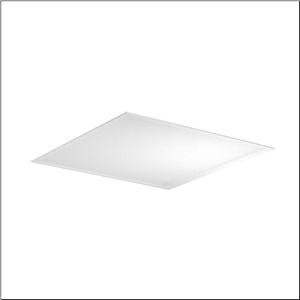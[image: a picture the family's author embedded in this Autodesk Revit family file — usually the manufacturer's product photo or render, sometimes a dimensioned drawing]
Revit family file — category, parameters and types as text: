
# Revit family: apollon_r__21_square_51mq12w72m14_a180
name_source: partatom
category: Lighting Fixtures
units: mm (PartAtom-declared; Revit-internal decimal feet)

## family parameters
Cut with Voids When Loaded = No
Host = Face
Light Source = No
Part Type = Normal
Room Calculation Point = No
Round Connector Dimension = Use Diameter
Shared = No

## types (1)
- --- (1 x LED, 4200 lm, 24.2 W, 4000K)
    Apparent Load = 24 VA
    CIE Flux Codes = 60 87 97 100 100
    Color Rendering = 80
    Color Temperature = 4000K
    Default Elevation = 1800 mm
    Description = Apollon® 21 square, office luminaire, primary optical cover: micro prismatic cover, of PMMA, CAT 2 (L<= 3000cd/m²), light emission: direct distribution, primary light characteristic: symmetric, installation type: lay-in mounting, LED, rated luminous flux: 4.200lm, luminous efficacy: 174lm/W, light colour: 830/840, colour temperature: 3000/4000K, with terminal, 3-pole, mains connection: 220..240V, AC/DC, 0/50..60Hz, rated input power: 24.2W, housing, of aluminium, coated, traffic white (RAL 9016), module: M600, length: 595mm, width: 595mm, height: 30mm, housing upper side, of sheet steel, galvanised, protection rating (complete): IP20, protection rating (lamp compartment, on room side): IP50, insulation class (complete): insulation class II (safety insulation), certification: CE, ENEC, impact resistance: IK03, permissible operating ambient temperature: -20..+45°C, permissible storage temperature: -40..+80°C, packaging unit: 1 piece
    Height = 0 mm  [stored 0 ft]
    Lamp = 1 x LED
    Lamp Light Flux = 4200 lm
    Lamp Power = 24.2 W
    Lamp count = 1
    Length = 595 mm
    Luminous efficacy = 174 lm/W
    Manufacturer = Siteco
    ModVariant = No
    Model = 51MQ12W72M14
    Mounting Place = Ceiling
    Mounting Type = Recessed
    Number of Poles = 1
    OnlyDefault = Yes
    Power Factor = 1
    Product Name = Apollon® 21 square
    Product group = office luminaire | ceiling recessed
    ProductGroupID = 400
    Protection Class = Protection class II
    Protection Degree = IP 20
    RLX_Detail_Level = 1
    RLX_Emergency_Light_Flux = 0 lm
    RLX_Emergency_Type = 0
    RLX_Emergency_Type_DB = No
    RlxData = <blob elided: 12709 chars, md5=1cea54f9>
    Socket = socket
    Standby Power = 0 W
    System Light Flux = 4200 lm
    System Power = 24 W
    Type Comments = factory setting
    Type Image = l_1291049.jpg
    URL = http://relux.com
    VarID = @adj_036399
    Voltage = 0 V
    Weight = 0.00 kg
    Width = 595 mm

note: [stored X ft] marks values corroborated as IEEE doubles in the binary element streams (Revit-internal decimal feet)

## geometry (parser evidence)
native form markers: Sweep x10
no freeform markers — native parametric forms only
